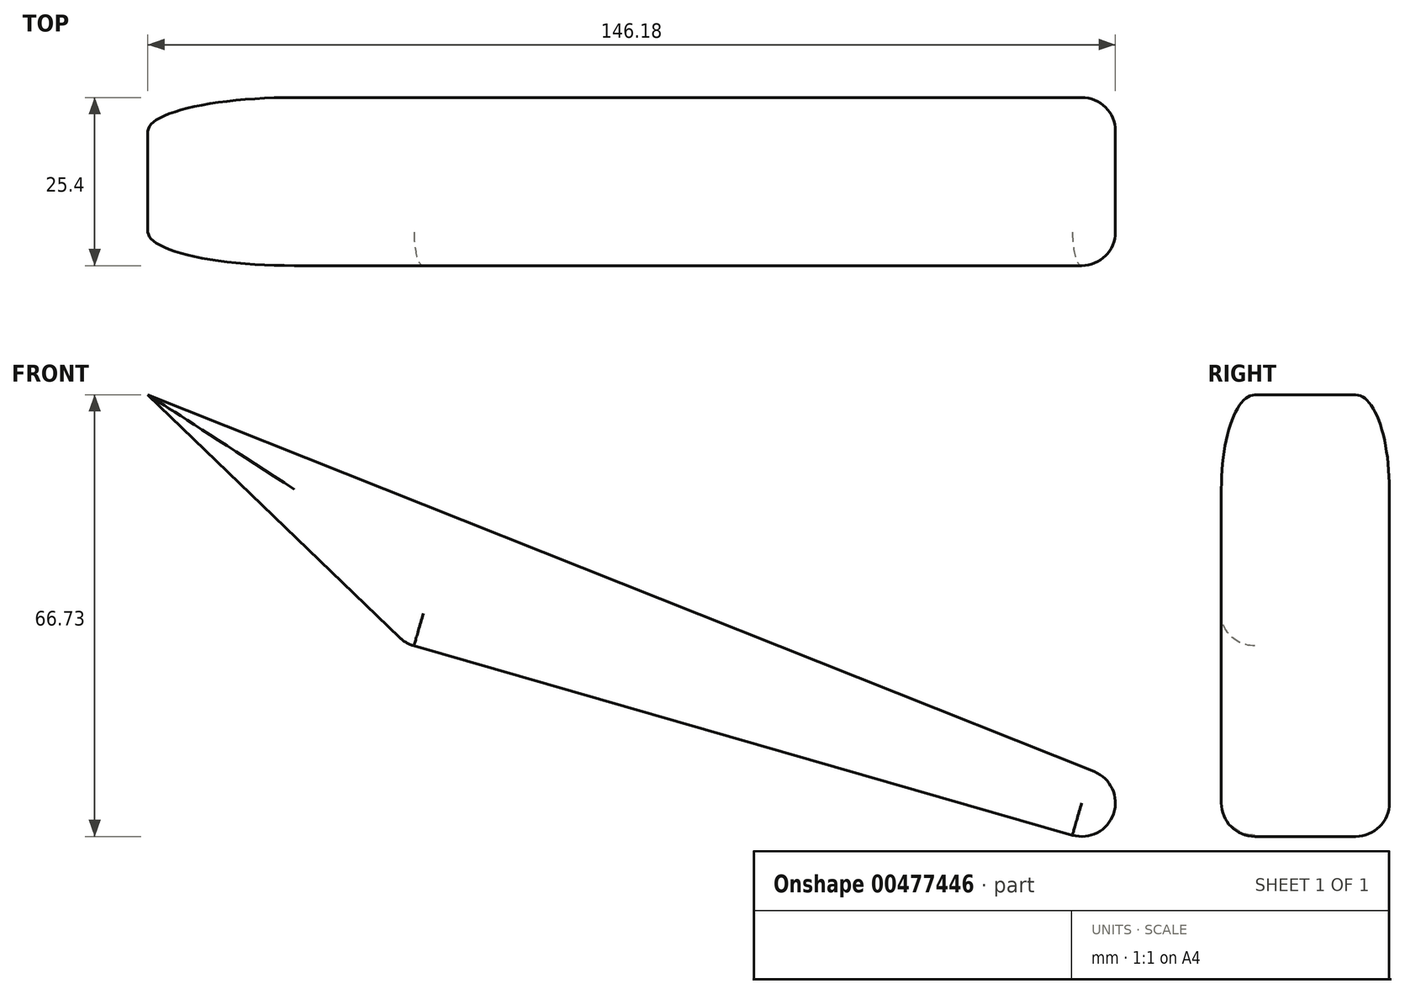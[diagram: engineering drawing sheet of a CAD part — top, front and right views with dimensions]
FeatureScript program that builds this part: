
annotation { "Feature Type Name" : "Feature", "Feature Type Description" : "" }
export const myFeature = defineFeature(function(context is Context, id is Id, definition is map)
    precondition{}
    {
        {
            var Q0;
            Q0=qCreatedBy(makeId("Front.planeOp"),FACE);
            var sketch = newSketch(context, id + "F0", { "sketchPlane" : qUnion([Q0])});
            skLineSegment(sketch, "E0", {"start": v(-39, 37.6) * mm, "end": v(0, 0) * mm});
            skLineSegment(sketch, "E1", {"start": v(199.19, -57.26) * mm, "end": v(0, 0) * mm});
            skLineSegment(sketch, "E2", {"start": v(199.19, -57.26) * mm, "end": v(-39, 37.6) * mm});
            skSolve(sketch);
        }
        {
            var Q0;
            Q0 = qSketchRegion(id + "F0", true);
            extrude(context, id + "F1", {"entities" : qUnion([Q0]), "depth" : 25.4 * mm});
        }
        {
            var Q0;
            Q0=makeQuery(id+"F1.opExtrude","CAP_EDGE",EDGE,{"disambiguationData":[OSD([sQuery(id+"F0.wireOp",EDGE,"E1")])],"isStart":false});
            fillet(context, id + "F2", {"entities" : qUnion([Q0]), "radius" : 5.08 * mm, "tangentPropagation" : true, "allowEdgeOverflow" : false});
        }
        {
            var Q0;
            Q0=makeQuery(id+"F2.opFillet","BLEND_FACE",FACE,{"disambiguationData":[OSD([sQuery(id+"F0.wireOp",EDGE,"E1")])]});
            var Q1;
            Q1=makeQuery(id+"F1.opExtrude","CAP_FACE",FACE,{"disambiguationData":[OSD([sQuery(id+"F0.wireOp",EDGE,"E0"),sQuery(id+"F0.wireOp",EDGE,"E1"),sQuery(id+"F0.wireOp",EDGE,"E2")])],"isStart":false});
            var Q2;
            Q2=makeQuery(id+"F1.opExtrude","SWEPT_FACE",FACE,{"disambiguationData":[OSD([sQuery(id+"F0.wireOp",EDGE,"E1")])]});
            var Q3;
            Q3=makeQuery(id+"F1.opExtrude","CAP_EDGE",EDGE,{"disambiguationData":[OSD([sQuery(id+"F0.wireOp",EDGE,"E1")])],"isStart":true});
            var Q4;
            Q4=makeQuery(id+"F1.opExtrude","CAP_FACE",FACE,{"disambiguationData":[OSD([sQuery(id+"F0.wireOp",EDGE,"E0"),sQuery(id+"F0.wireOp",EDGE,"E1"),sQuery(id+"F0.wireOp",EDGE,"E2")])],"isStart":true});
            var Q5;
            {var subQ0=sQuery(id+"F0.wireOp",EDGE,"E1");Q5=makeQuery(id+"F2.opFillet","BLEND_EDGE",EDGE,{"blendedFrom":[makeQuery(id+"F1.opExtrude","CAP_EDGE",EDGE,{"disambiguationData":[OSD([subQ0])],"isStart":false}),makeQuery(id+"F1.opExtrude","SWEPT_FACE",FACE,{"disambiguationData":[OSD([subQ0])]})],"blendedInto":[makeQuery(id+"F1.opExtrude","SWEPT_FACE",FACE,{"disambiguationData":[OSD([subQ0])]})]});}
            fillet(context, id + "F3", {"entities" : qUnion([Q0, Q1, Q2, Q3, Q4, Q5]), "radius" : 5.08 * mm, "tangentPropagation" : true, "allowEdgeOverflow" : false});
        }
    });
